# Revit family: REVIT-Ladders-LD51
name_source: partatom
category: Specialty Equipment
revit_build: Autodesk Revit 2016 (Build: 20150714_1515(x64)
units: mm (PartAtom-declared; Revit-internal decimal feet)

## family parameters
Always vertical = Yes
Cut with Voids When Loaded = No
Part Type = Normal
Room Calculation Point = No
Round Connector Dimension = Use Diameter
Shared = No
Work Plane-Based = No

## types (4) — shared parameters
Assembly Code = B1010700
Manufacturer = Monkey Toe Group Limited
Material = Metal_Ladders_Aluminium
MaterialPerforated = Metal_Ladders_Aluminium_Perforated
Model = LD51
ModifiedIssue_ANZRS = 20160712 $

## per-type parameters (varying)
| type | Description | SupportLanding | SupportLandingOffset | URL | VerticalHeightMaximum | VerticalHeightMinimum |
| Type 1 - Flat Surface to Roof Deck | Vertical Line Ladder with Grabrails, and 1.0m Landing | No | 0 mm  [stored 0 ft] | http://www.monkeytoe.co.nz | 5700 mm  [stored 18.7008 ft] | 3300 mm  [stored 10.8268 ft] |
| Type 2 - Roof Deck to Roof Deck | Vertical Line Ladder with Grabrails, 1.0m Landing, and Support Landing | Yes | 77 mm | www.sayfa.com.au | 5700 mm  [stored 18.7008 ft] | 3300 mm  [stored 10.8268 ft] |
| Type 1 - Flat Surface to Roof Deck with Midway Rest Platform | Vertical Line Ladder with Grabrails, Midway Rest Platform, and 1.0m Landing | No | 0 mm  [stored 0 ft] | www.sayfa.com.au | 11700 mm  [stored 38.3858 ft] | 6900 mm  [stored 22.6378 ft] |
| Type 2 - Roof Deck to Roof Deck with Midway Rest Platform | Vertical Line Ladder with Grabrails, Midway Rest Platform, 1.0m Landing, and Support Landing | Yes | 77 mm | www.sayfa.com.au | 11700 mm  [stored 38.3858 ft] | 6900 mm  [stored 22.6378 ft] |

note: [stored X ft] marks values corroborated as IEEE doubles in the binary element streams (Revit-internal decimal feet)

## geometry (parser evidence)
native form markers: Sweep x23
no freeform markers — native parametric forms only
